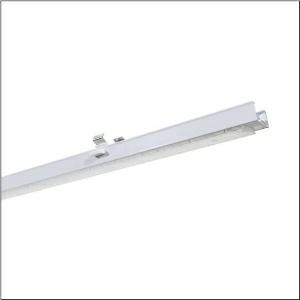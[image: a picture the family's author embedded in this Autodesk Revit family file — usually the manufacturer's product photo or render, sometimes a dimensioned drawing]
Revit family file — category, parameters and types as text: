
# Revit family: sanierungs-leuchteneinsatz_31_gen_2_51re18ma46b_eee1
name_source: partatom
category: Lighting Fixtures
units: mm (PartAtom-declared; Revit-internal decimal feet)

## family parameters
Cut with Voids When Loaded = No
Host = Face
Light Source = No
Part Type = Normal
Room Calculation Point = No
Round Connector Dimension = Use Diameter
Shared = No

## types (1)
- --- (1 x LED, 6400 lm, 40 W, 4000K)
    Apparent Load = 40 VA
    CIE Flux Codes = 71 89 97 97 100
    Color Rendering = 80
    Color Temperature = 4000K
    Default Elevation = 1800 mm
    Description = Refurbishment luminaire insert Gen.2, luminaire insert, of extruded aluminium section, coated, traffic white (RAL 9016), length: 1.172mm, width: 91mm, height: 53mm, LED rated luminous flux: 6.400lm, light colour: 840, control gear: ON/OFF Multilumen, control gear: ECG Multilumen, with system connector: socket, mains connection: 220..240V, AC/DC, 0/50..60Hz, luminous flux adjustable on luminaire in four steps (3420/4540/5580/6630lm), connected load according to luminous flux setting (20/26/33/40W), primary light control with lens, of plastic, primary optical cover: cover, of PMMA, light emission: direct distribution, protection rating (complete): IP20, insulation class (complete): insulation class I (protective earthing), certification: CE, UKCA, permissible ambient temperature for indoor applications: -20..+40°C, packaging unit: 1 piece
    Height = 58 mm
    Lamp = 1 x LED
    Lamp Light Flux = 6400 lm
    Lamp Power = 40 W
    Lamp count = 1
    Length = 1172 mm
    Luminous efficacy = 160 lm/W
    Manufacturer = Siteco
    ModVariant = No
    Model = 51RE18MA46B
    Mounting Place = Ceiling
    Mounting Type = Pendant
    Number of Poles = 1
    OnlyDefault = Yes
    Power Factor = 1
    Product Name = Sanierungs-Leuchteneinsatz 31 Gen.2
    Product group = luminaire insert
    ProductGroupID = 902
    Protection Class = Protection class I
    Protection Degree = IP 20
    RLX_Detail_Level = 1
    RlxData = <blob elided: 20013 chars, md5=8d47f784>
    Socket = socket
    Standby Power = 0 W
    System Light Flux = 6400 lm
    System Power = 40 W
    Type Comments = factory setting: luminous flux: 100 % | (ON | ON) | 300 mA
    Type Image = l_1266702.jpg
    URL = http://relux.com
    VarID = @adj_089637
    Voltage = 0 V
    Weight = 0.00 kg
    Width = 65 mm

## geometry (parser evidence)
native form markers: Blend x4, Sweep x12
no freeform markers — native parametric forms only
